# Revit family: CurtainPanel_OperableWall_AdvancedEQ_SingleDoor
name_source: partatom
category: Curtain Panels
units: mm (PartAtom-declared; Revit-internal decimal feet)

## family parameters
Always vertical = Yes
Cut with Voids When Loaded = No
Shared = No

## types (1)
- CurtainPanel_OperableWall_AdvancedEQ_SingleDoor
    Assembly Code = B2020220
    BaseGap = 0' - 3"
    Description = Advanced Equipment Moving Panel as Specified
    Door Height = 7' - 0"
    Door Width = 3' - 0"
    Expected Lifespan (Years) = 0
    Frame Material = Metal - Aluminum - Advanced EQ - Anodized - Clear
    Green Building-LEED = http://www.advancedequipment.com
    Keynote = 10650
    Maintenance Schedule (Months) = 0
    Manufacturer = Advanced Equipment Corp.
    Manufacturer Fax = 714-525-6083
    Manufacturer Website = http://www.advancedequipment.com
    Max Height = 0' - 0"
    Max Width = 0' - 0"
    Model = As Specified
    Noise Reduction Coefficient (NRC) = 0
    Product Data = http://arcat.com
    Revision = R1_04-2013
    Sales Information = http://www.advancedequipment.com
    Send Message = http://www.arcat.com
    Sound Transmission Class (STC) = 0
    Specification = http://arcat.com
    URL = http://www.advancedequipment.com
    Unit Depth = 0' - 4"
    Vision Lite Height = 2' - 6"
    Vision Lite Width = 0' - 8"
    Warranty Duration (Years) = 0

## geometry (parser evidence)
native form markers: Blend x46, Sweep x6
no freeform markers — native parametric forms only
